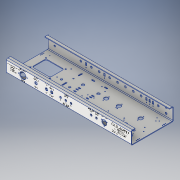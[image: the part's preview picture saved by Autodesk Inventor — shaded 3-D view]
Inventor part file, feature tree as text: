
AUTODESK INVENTOR PART (.ipt)
format: ipt  version: 2018.3 (Build 223285000, 285)  size: 2,179,584 bytes
history: native  units: in
note: dims shown in document units (in); Inventor stores cm internally (conversion verified against a paired STEP export)
features: other x16, sheet_metal_op x13, sketch x10
ambient origin geometry x8: Origin, YZ Plane, XZ Plane, XY Plane, X Axis, Y Axis, Z Axis, Center Point
bodies: Solid1 (feature_tree)
feature tree (39):
  sheet_metal_op  "Face1"
  sketch  "Sketch2"  dims[d0=23.75in]
  sheet_metal_op  "Flange1"
  sheet_metal_op  "Flange2"
  sheet_metal_op  "Flange3"
  sheet_metal_op  "Flange4"
  other  "Decal1"
  other  "Decal2"
  sketch  "Sketch11"  dims[d13=0.125in d14=0.125in d17=0.125in d18=0.0625in d19=0.25in d20=0.125in d21=0.75in d22=90.0deg d23=0.125in d24=0.5in d25=0.125in d26=0.125in d27=0.125in d28=0.0in d29=0.125in d30=0.0625in d31=0.25in d32=0.125in d33=2.5in d34=90.0deg d35=0.125in d36=0.5in d37=0.125in d38=0.125in d39=0.125in d40=0.0625in d41=0.25in d42=0.125in d43=0.75in d44=90.0deg d45=0.125in d46=0.5in d47=0.125in d48=0.125in d49=0.125in d50=0.0in d439=0.125in d440=0.0in]
  other  "Plate1"
  sketch  "Sketch3"  dims[d1=8.05in]
  other  "Plate2"
  sheet_metal_op  "Bend1"
  sheet_metal_op  "Corner1"
  sketch  "Sketch4"  dims[d2=0.125in]
  other  "Plate3"
  sheet_metal_op  "Bend2"
  sheet_metal_op  "Corner2"
  sketch  "Sketch5"  dims[d5=0.125in]
  sketch  "Sketch6"  dims[d6=0.0625in]
  other  "Plate4"
  sheet_metal_op  "Bend3"
  sheet_metal_op  "Corner3"
  sketch  "Sketch7"  dims[d7=0.25in]
  other  "Plate5"
  sheet_metal_op  "Bend4"
  sheet_metal_op  "Corner4"
  sketch  "Sketch8"  dims[d8=0.125in]
  sketch  "Sketch9"  dims[d9=2.5in d10=90.0deg d11=0.125in]
  sketch  "Sketch10"  dims[d12=0.5in]
  other  "Image6"
  other  "Image7"
  other  "Image8"
  other  "Image18"
  other  "Image20"
  other  "Cut2"
  other  "Cut3"
  other  "Cut4"
  other  "Definition1"
